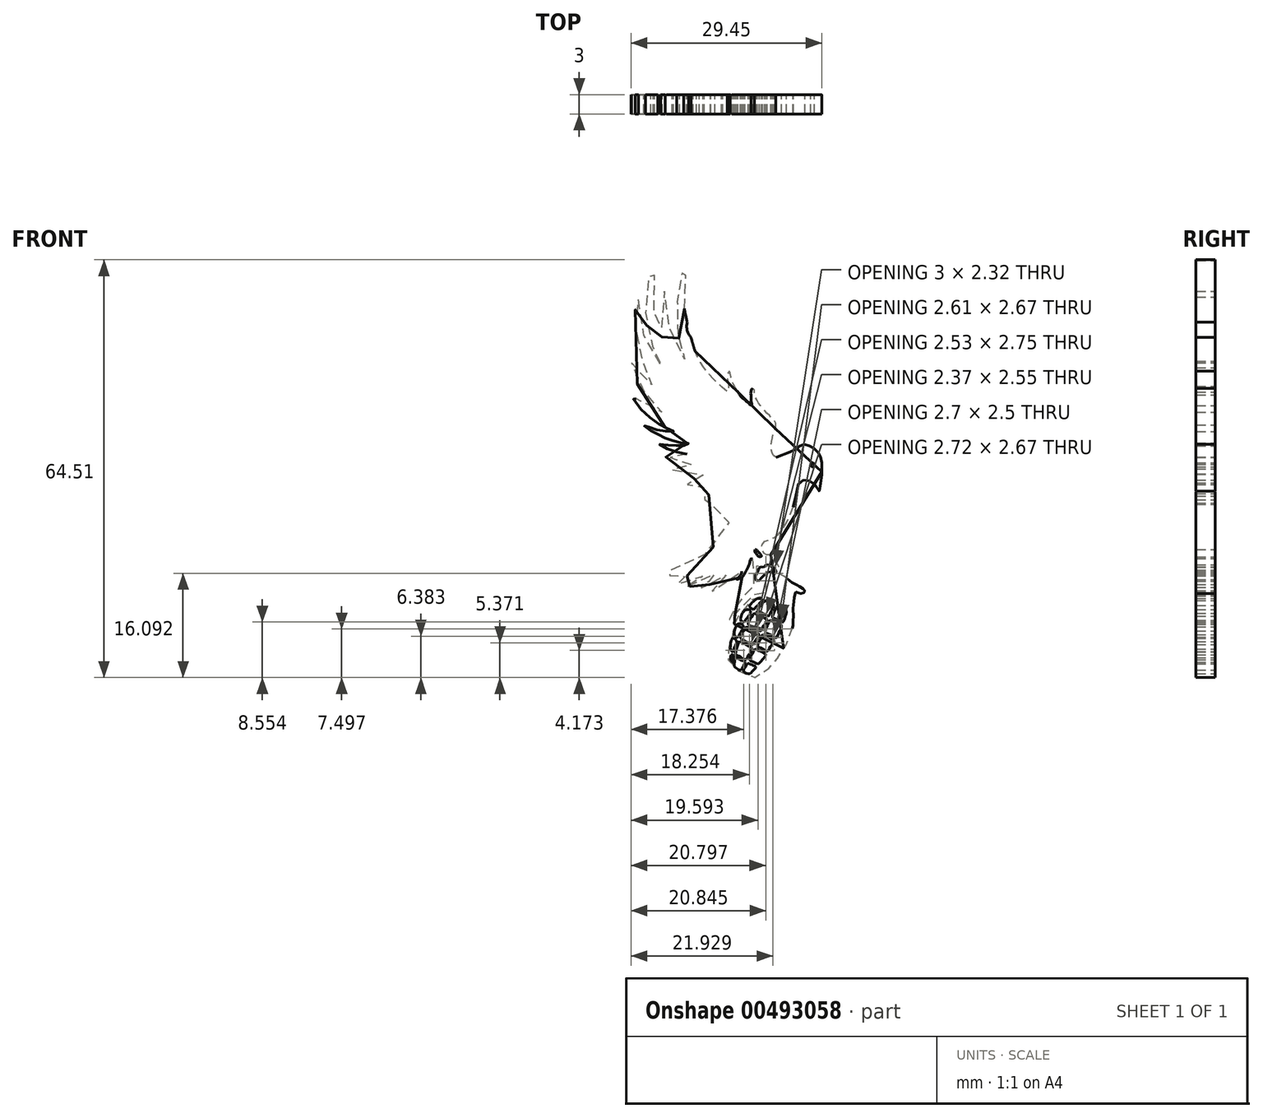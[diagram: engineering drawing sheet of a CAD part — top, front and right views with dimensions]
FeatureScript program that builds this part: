
annotation { "Feature Type Name" : "Feature", "Feature Type Description" : "" }
export const myFeature = defineFeature(function(context is Context, id is Id, definition is map)
    precondition{}
    {
        {
            var Q0;
            Q0=qCreatedBy(makeId("Front.planeOp"),FACE);
            var sketch = newSketch(context, id + "F0", { "sketchPlane" : qUnion([Q0])});
            skFitSpline(sketch, "E0", {"points": [v(10.7, -6.54) * mm, v(10.82, -6.51) * mm, v(10.87, -6.35) * mm, v(10.83, -6.15) * mm, v(10.74, -5.98) * mm, v(10.6, -5.9) * mm, v(10.46, -5.88) * mm, v(10.34, -5.97) * mm, v(10.3, -6.12) * mm, v(10.31, -6.28) * mm, v(10.4, -6.45) * mm, v(10.48, -6.53) * mm, v(10.58, -6.56) * mm, v(10.7, -6.54) * mm]});
            skFitSpline(sketch, "E1", {"points": [v(1.69, -19.3) * mm, v(1.72, -19.8) * mm, v(1.94, -20.05) * mm, v(2.26, -20.4) * mm, v(2.65, -20.35) * mm, v(2.45, -19.97) * mm, v(2.16, -19.65) * mm, v(1.98, -19.4) * mm, v(1.69, -19.3) * mm]});
            skFitSpline(sketch, "E2", {"points": [v(1.88, -24.14) * mm, v(2.38, -24.05) * mm, v(2.74, -23.63) * mm, v(3.12, -23.22) * mm, v(3.52, -22.85) * mm, v(4.1, -22.72) * mm, v(4.6, -23) * mm, v(4.85, -23) * mm, v(4.9, -22.66) * mm, v(4.72, -22.26) * mm, v(4.44, -22) * mm, v(4.24, -21.9) * mm, v(3.88, -21.74) * mm, v(3.66, -21.64) * mm, v(3.38, -21.69) * mm, v(3.17, -21.9) * mm, v(2.98, -22) * mm, v(2.7, -22) * mm, v(2.47, -22) * mm, v(2.33, -22.16) * mm, v(2.18, -22.42) * mm, v(2.05, -22.66) * mm, v(1.94, -22.9) * mm, v(1.84, -23.17) * mm, v(1.77, -23.51) * mm, v(1.75, -23.84) * mm, v(1.88, -24.14) * mm]});
            skFitSpline(sketch, "E3", {"points": [v(5.15, -28) * mm, v(5.57, -28.06) * mm, v(6.04, -28.28) * mm, v(6.42, -28.52) * mm, v(6.48, -29.14) * mm, v(6.34, -29.66) * mm, v(6.18, -30.2) * mm, v(5.94, -30.52) * mm, v(5.51, -30.4) * mm, v(4.93, -30.1) * mm, v(4.53, -29.9) * mm, v(4.33, -29.74) * mm, v(4.51, -29.24) * mm, v(4.77, -28.66) * mm, v(5.15, -28) * mm]});
            skFitSpline(sketch, "E4", {"points": [v(2.05, -28.66) * mm, v(2.3, -28.25) * mm, v(2.68, -27.77) * mm, v(3.02, -27.43) * mm, v(3.32, -27.2) * mm, v(3.73, -27.25) * mm, v(4.05, -27.47) * mm, v(4.4, -27.69) * mm, v(4.59, -27.92) * mm, v(4.43, -28.36) * mm, v(4.2, -28.78) * mm, v(4, -29.15) * mm, v(3.8, -29.56) * mm, v(3.38, -29.45) * mm, v(3.04, -29.27) * mm, v(2.73, -29.09) * mm, v(2.43, -28.96) * mm, v(2.16, -28.8) * mm, v(2.05, -28.66) * mm]});
            skFitSpline(sketch, "E5", {"points": [v(1.48, -28.57) * mm, v(1.77, -28.2) * mm, v(2.04, -27.96) * mm, v(2.29, -27.68) * mm, v(2.55, -27.44) * mm, v(2.85, -27.12) * mm, v(2.77, -26.92) * mm, v(2.39, -26.88) * mm, v(2.05, -26.86) * mm, v(1.73, -27.08) * mm, v(1.39, -27.37) * mm, v(1.14, -27.6) * mm, v(0.9, -27.86) * mm, v(0.83, -28.12) * mm, v(1.02, -28.34) * mm, v(1.33, -28.5) * mm, v(1.48, -28.57) * mm]});
            skFitSpline(sketch, "E6", {"points": [v(-0.02, -30.5) * mm, v(0.21, -30.2) * mm, v(0.43, -29.88) * mm, v(0.71, -29.5) * mm, v(0.92, -29.16) * mm, v(0.96, -28.8) * mm, v(0.73, -28.6) * mm, v(0.4, -28.56) * mm, v(0.15, -28.66) * mm, v(-0.09, -28.9) * mm, v(-0.34, -29.28) * mm, v(-0.5, -29.66) * mm, v(-0.57, -30) * mm, v(-0.52, -30.25) * mm, v(-0.26, -30.44) * mm, v(-0.02, -30.5) * mm]});
            skFitSpline(sketch, "E7", {"points": [v(1.52, -29.18) * mm, v(1.88, -29.3) * mm, v(2.23, -29.46) * mm, v(2.56, -29.6) * mm, v(2.9, -29.78) * mm, v(3.23, -29.94) * mm, v(3.54, -30.13) * mm, v(3.37, -30.52) * mm, v(3.17, -30.8) * mm, v(3, -31.1) * mm, v(2.84, -31.4) * mm, v(2.7, -31.7) * mm, v(2.54, -31.9) * mm, v(2.15, -31.76) * mm, v(1.8, -31.6) * mm, v(1.46, -31.4) * mm, v(1.17, -31.29) * mm, v(0.88, -31.1) * mm, v(0.62, -30.86) * mm, v(0.66, -30.42) * mm, v(0.9, -30.07) * mm, v(1.15, -29.7) * mm, v(1.33, -29.4) * mm, v(1.52, -29.18) * mm]});
            skFitSpline(sketch, "E8", {"points": [v(3.15, -31.96) * mm, v(3.32, -31.47) * mm, v(3.58, -31) * mm, v(3.78, -30.61) * mm, v(4, -30.24) * mm, v(4.47, -30.43) * mm, v(4.79, -30.58) * mm, v(5.24, -30.76) * mm, v(5.73, -30.95) * mm, v(5.68, -31.5) * mm, v(5.46, -31.96) * mm, v(5.26, -32.43) * mm, v(4.96, -32.9) * mm, v(4.45, -32.73) * mm, v(3.91, -32.43) * mm, v(3.56, -32.26) * mm, v(3.15, -31.96) * mm]});
            skFitSpline(sketch, "E9", {"points": [v(1.98, -34.15) * mm, v(2.22, -33.67) * mm, v(2.42, -33.25) * mm, v(2.7, -32.72) * mm, v(2.9, -32.45) * mm, v(3.37, -32.6) * mm, v(3.74, -32.82) * mm, v(4.1, -33) * mm, v(4.45, -33.21) * mm, v(4.68, -33.37) * mm, v(4.48, -33.72) * mm, v(4.24, -34.08) * mm, v(4, -34.42) * mm, v(3.79, -34.75) * mm, v(3.57, -35.03) * mm, v(3.13, -34.83) * mm, v(2.72, -34.6) * mm, v(2.26, -34.36) * mm, v(1.98, -34.15) * mm]});
            skFitSpline(sketch, "E10", {"points": [v(1.36, -33.96) * mm, v(1.55, -33.63) * mm, v(1.82, -33.21) * mm, v(2.09, -32.82) * mm, v(2.34, -32.43) * mm, v(2.04, -32.2) * mm, v(1.67, -32) * mm, v(1.37, -31.8) * mm, v(0.97, -31.58) * mm, v(0.66, -31.38) * mm, v(0.38, -31.25) * mm, v(0.1, -31.44) * mm, v(-0.09, -31.79) * mm, v(-0.19, -32.05) * mm, v(-0.32, -32.34) * mm, v(-0.45, -32.65) * mm, v(-0.6, -32.95) * mm, v(-0.38, -33.15) * mm, v(-0.13, -33.32) * mm, v(0.13, -33.47) * mm, v(0.43, -33.64) * mm, v(0.7, -33.8) * mm, v(1.02, -33.96) * mm, v(1.36, -33.96) * mm]});
            skFitSpline(sketch, "E11", {"points": [v(-0.93, -32.84) * mm, v(-0.75, -32.41) * mm, v(-0.5, -31.97) * mm, v(-0.26, -31.57) * mm, v(-0.12, -31.22) * mm, v(-0.38, -30.85) * mm, v(-0.76, -30.76) * mm, v(-1.13, -30.91) * mm, v(-1.4, -31.42) * mm, v(-1.53, -31.91) * mm, v(-1.56, -32.32) * mm, v(-1.44, -32.67) * mm, v(-1.13, -32.83) * mm, v(-0.93, -32.84) * mm]});
            skFitSpline(sketch, "E12", {"points": [v(-1.73, -35.1) * mm, v(-1.55, -34.61) * mm, v(-1.36, -34.12) * mm, v(-1.16, -33.6) * mm, v(-1.33, -33.18) * mm, v(-1.78, -33.04) * mm, v(-2.07, -33.52) * mm, v(-2.12, -34.19) * mm, v(-2.1, -34.76) * mm, v(-1.73, -35.1) * mm]});
            skFitSpline(sketch, "E13", {"points": [v(-2.02, -35.59) * mm, v(-1.68, -35.6) * mm, v(-1.7, -36.13) * mm, v(-1.76, -36.7) * mm, v(-2.02, -36.45) * mm, v(-2.1, -36) * mm, v(-2.02, -35.59) * mm]});
            skFitSpline(sketch, "E14", {"points": [v(-1.52, -37.35) * mm, v(-1.54, -36.94) * mm, v(-1.47, -36.36) * mm, v(-1.27, -36.03) * mm, v(-0.79, -36.22) * mm, v(-0.42, -36.43) * mm, v(0.1, -36.57) * mm, v(-0.04, -37.14) * mm, v(-0.23, -37.52) * mm, v(-0.45, -37.89) * mm, v(-0.83, -37.9) * mm, v(-1.16, -37.66) * mm, v(-1.52, -37.35) * mm]});
            skFitSpline(sketch, "E15", {"points": [v(0.54, -36.88) * mm, v(0.91, -36.98) * mm, v(1.35, -37.18) * mm, v(1.79, -37.42) * mm, v(1.58, -37.8) * mm, v(1.24, -38.11) * mm, v(0.88, -38.47) * mm, v(0.46, -38.47) * mm, v(0.06, -38.28) * mm, v(-0.1, -37.99) * mm, v(0.16, -37.48) * mm, v(0.37, -37.08) * mm, v(0.54, -36.88) * mm]});
            skFitSpline(sketch, "E16", {"points": [v(0.8, -36.26) * mm, v(1.04, -35.8) * mm, v(1.27, -35.35) * mm, v(1.55, -34.8) * mm, v(1.8, -34.68) * mm, v(2.32, -34.92) * mm, v(2.85, -35.17) * mm, v(3.33, -35.51) * mm, v(3.1, -35.98) * mm, v(2.82, -36.3) * mm, v(2.56, -36.62) * mm, v(2.18, -36.98) * mm, v(1.7, -36.83) * mm, v(1.3, -36.63) * mm, v(0.8, -36.26) * mm]});
            skFitSpline(sketch, "E17", {"points": [v(0.3, -36.27) * mm, v(0.54, -35.85) * mm, v(0.85, -35.37) * mm, v(1.1, -34.87) * mm, v(1.18, -34.51) * mm, v(0.67, -34.18) * mm, v(0.15, -33.9) * mm, v(-0.26, -33.6) * mm, v(-0.8, -33.55) * mm, v(-1.02, -34.06) * mm, v(-1.21, -34.7) * mm, v(-1.29, -35.13) * mm, v(-1.33, -35.55) * mm, v(-0.85, -35.76) * mm, v(-0.38, -36.01) * mm, v(0, -36.26) * mm, v(0.3, -36.27) * mm]});
            skCircle(sketch, "E18", {"center": v(-6.39, 15.14) * mm, "radius": 2.5 * mm});
            skArc(sketch, "E19.trimOffspring", {"start": v(-7.61, 11.37) * mm, "mid": v(-2.47, 16.13) * mm, "end": v(-9.25, 17.92) * mm});
            skFitSpline(sketch, "E20.trimOffspring", {"points": [v(11.64, -10.29) * mm, v(11.75, -9.58) * mm, v(11.84, -8.7) * mm, v(11.95, -7.88) * mm, v(11.98, -7.17) * mm, v(11.98, -6.38) * mm, v(11.9, -5.44) * mm, v(11.67, -4.74) * mm, v(11.3, -4.23) * mm, v(10.7, -3.66) * mm, v(10.17, -3.38) * mm, v(9.6, -3.15) * mm, v(8.86, -3.1) * mm, v(8.36, -3.52) * mm, v(7.85, -3.91) * mm, v(7.28, -4.17) * mm, v(6.6, -4.42) * mm, v(6, -4.65) * mm, v(5.5, -4.85) * mm, v(4.87, -5.1) * mm, v(4.52, -4.8) * mm, v(4.3, -4.37) * mm, v(4.17, -3.82) * mm, v(4.15, -3.18) * mm, v(4.23, -2.52) * mm, v(4.37, -1.93) * mm, v(4.52, -1.4) * mm, v(4.75, -0.8) * mm, v(4.89, -0.23) * mm, v(4.84, 0.33) * mm, v(4.57, 0.7) * mm, v(4.26, 1.02) * mm, v(3.93, 1.36) * mm, v(3.6, 1.69) * mm, v(3.22, 2.1) * mm, v(2.9, 2.47) * mm, v(2.59, 2.8) * mm, v(2.31, 3.17) * mm, v(2.06, 3.59) * mm, v(1.84, 4) * mm, v(1.62, 4.41) * mm, v(1.57, 4.92) * mm, v(1.5, 5.5) * mm, v(1.28, 5.6) * mm, v(1.05, 5.15) * mm, v(1.05, 4.48) * mm, v(1.05, 3.84) * mm, v(1.17, 3.24) * mm, v(1.1, 2.93) * mm, v(0.71, 3.25) * mm, v(0.4, 3.49) * mm, v(0.12, 3.74) * mm, v(-0.2, 4) * mm, v(-0.45, 4.22) * mm, v(-0.65, 4.48) * mm, v(-0.85, 4.87) * mm, v(-1.16, 5.33) * mm, v(-1.45, 5.8) * mm, v(-1.72, 6.3) * mm, v(-1.94, 6.85) * mm, v(-2.08, 7.45) * mm, v(-2.17, 7.99) * mm, v(-2.18, 8.21) * mm, v(-2.5, 8.19) * mm, v(-2.6, 7.62) * mm, v(-2.58, 7.01) * mm, v(-2.5, 6.46) * mm, v(-2.44, 5.92) * mm, v(-2.41, 5.34) * mm, v(-2.45, 5.03) * mm, v(-2.78, 5.25) * mm, v(-3.2, 5.57) * mm, v(-3.68, 6.02) * mm, v(-4.14, 6.43) * mm, v(-4.56, 6.83) * mm, v(-5.11, 7.45) * mm, v(-5.77, 8.16) * mm, v(-6.28, 8.86) * mm, v(-6.84, 9.77) * mm, v(-7.4, 10.79) * mm, v(-9.28, 18.06) * mm, v(-9.32, 19.16) * mm, v(-9.28, 20.44) * mm, v(-9.2, 21.85) * mm, v(-9.01, 23.04) * mm, v(-8.79, 24.45) * mm, v(-8.64, 25.44) * mm, v(-9.16, 24.68) * mm, v(-9.48, 23.78) * mm, v(-9.78, 22.92) * mm, v(-10, 22.06) * mm, v(-10.16, 21.07) * mm, v(-10.26, 20.05) * mm, v(-10.32, 19.15) * mm, v(-10.39, 18.06) * mm, v(-10.44, 16.91) * mm, v(-10.44, 15.82) * mm, v(-10.34, 14.53) * mm, v(-10.06, 13.2) * mm, v(-9.72, 11.96) * mm, v(-9.25, 10.72) * mm, v(-8.87, 9.77) * mm, v(-9.58, 10.53) * mm, v(-10.39, 11.72) * mm, v(-10.91, 12.82) * mm, v(-11.44, 14.44) * mm, v(-11.72, 15.63) * mm, v(-12.06, 16.96) * mm, v(-12.25, 18.77) * mm, v(-12.3, 20.58) * mm, v(-12.77, 19.1) * mm, v(-12.87, 17.53) * mm, v(-12.82, 15.91) * mm, v(-12.77, 14.72) * mm, v(-12.77, 13.49) * mm, v(-13.39, 14.82) * mm, v(-13.77, 16.3) * mm, v(-14, 17.87) * mm, v(-14, 19.58) * mm, v(-13.96, 21.2) * mm, v(-13.92, 22.51) * mm, v(-13.64, 24.07) * mm, v(-13.36, 25.35) * mm, v(-14.08, 24.4) * mm, v(-14.56, 23.31) * mm, v(-15, 21.95) * mm, v(-15.12, 20.47) * mm, v(-15.2, 19.03) * mm, v(-15.24, 17.47) * mm, v(-15.16, 16.14) * mm, v(-14.96, 14.82) * mm, v(-14.64, 13.66) * mm, v(-14.24, 12.26) * mm, v(-13.68, 11.02) * mm, v(-13.2, 10.14) * mm, v(-12.68, 9.34) * mm, v(-12.28, 8.78) * mm, v(-13.12, 9.34) * mm, v(-13.88, 10.3) * mm, v(-14.52, 11.5) * mm, v(-15.12, 12.86) * mm, v(-15.68, 14.26) * mm, v(-16, 15.66) * mm, v(-16.24, 17.07) * mm, v(-16.36, 18.3) * mm, v(-16.4, 19.7) * mm, v(-16.76, 18.55) * mm, v(-16.8, 17.23) * mm, v(-16.84, 15.9) * mm, v(-16.76, 14.5) * mm, v(-16.6, 13.14) * mm, v(-16.32, 11.86) * mm, v(-15.88, 10.38) * mm, v(-15.56, 9.14) * mm, v(-15.04, 7.98) * mm, v(-14.4, 7.01) * mm, v(-13.84, 5.93) * mm, v(-14.76, 6.5) * mm, v(-15.52, 7.21) * mm, v(-16.16, 7.86) * mm, v(-16.92, 8.74) * mm, v(-17.4, 9.54) * mm, v(-17.28, 8.3) * mm, v(-16.92, 7.05) * mm, v(-16.28, 5.93) * mm, v(-15.71, 5.27) * mm, v(-15, 4.4) * mm, v(-14.43, 3.7) * mm, v(-13.8, 3.15) * mm, v(-13.19, 2.55) * mm, v(-12.65, 1.94) * mm, v(-13.56, 2.18) * mm, v(-14.23, 2.45) * mm, v(-15.17, 2.95) * mm, v(-15.91, 3.46) * mm, v(-16.76, 4.03) * mm, v(-17.46, 4.57) * mm, v(-16.72, 3.35) * mm, v(-16.12, 2.58) * mm, v(-15.3, 1.7) * mm, v(-14.4, 0.96) * mm, v(-13.6, 0.32) * mm, v(-12.81, -0.13) * mm, v(-12.24, -0.42) * mm, v(-11.8, -0.63) * mm, v(-11.35, -0.82) * mm, v(-10.92, -1.02) * mm, v(-11.31, -1.1) * mm, v(-11.9, -1.05) * mm, v(-12.44, -1.02) * mm, v(-13.08, -0.91) * mm, v(-13.67, -0.77) * mm, v(-14.29, -0.6) * mm, v(-14.81, -0.39) * mm, v(-15.2, -0.2) * mm, v(-15.54, -0.07) * mm, v(-15.27, -0.4) * mm, v(-14.9, -0.68) * mm, v(-14.46, -0.93) * mm, v(-14, -1.17) * mm, v(-13.5, -1.43) * mm, v(-13.03, -1.68) * mm, v(-12.62, -1.9) * mm, v(-12.09, -2.14) * mm, v(-11.66, -2.3) * mm, v(-11.16, -2.46) * mm, v(-10.59, -2.63) * mm, v(-10.12, -2.73) * mm, v(-9.56, -2.83) * mm, v(-9, -2.88) * mm, v(-8.56, -2.95) * mm, v(-8.66, -3.24) * mm, v(-9, -3.27) * mm, v(-9.42, -3.27) * mm, v(-9.94, -3.26) * mm, v(-10.38, -3.26) * mm, v(-10.87, -3.24) * mm, v(-11.44, -3.19) * mm, v(-12, -3.15) * mm, v(-12.5, -3.13) * mm, v(-13.14, -3.1) * mm, v(-12.5, -3.52) * mm, v(-11.68, -3.85) * mm, v(-10.84, -4.14) * mm, v(-9.98, -4.3) * mm, v(-9.15, -4.5) * mm, v(-8.3, -4.6) * mm, v(-7.87, -4.69) * mm, v(-8.2, -5) * mm, v(-8.96, -5.07) * mm, v(-9.53, -5.11) * mm, v(-10.27, -5.07) * mm, v(-10.96, -5.07) * mm, v(-11.44, -5.07) * mm, v(-12.25, -5.07) * mm, v(-11.53, -5.64) * mm, v(-11.1, -5.85) * mm, v(-10.39, -5.97) * mm, v(-9.48, -6.07) * mm, v(-8.65, -6.16) * mm, v(-8.03, -6.16) * mm, v(-7.39, -6.16) * mm, v(-7.65, -6.57) * mm, v(-8.27, -6.76) * mm, v(-8.91, -6.85) * mm, v(-9.84, -6.88) * mm, v(-10.53, -6.88) * mm, v(-11.13, -6.97) * mm, v(-10.53, -7.35) * mm, v(-9.91, -7.61) * mm, v(-9.08, -7.7) * mm, v(-8.25, -7.69) * mm, v(-7.41, -7.69) * mm, v(-6.72, -7.64) * mm, v(-6.37, -7.78) * mm, v(-6.87, -8.02) * mm, v(-7.5, -8.26) * mm, v(-8.08, -8.47) * mm, v(-8.8, -8.7) * mm, v(-9.34, -8.85) * mm, v(-9.98, -8.97) * mm, v(-8.98, -9.23) * mm, v(-7.94, -9.23) * mm, v(-7.08, -9.19) * mm, v(-6.32, -9.11) * mm, v(-5.75, -9.04) * mm, v(-5.15, -9.11) * mm, v(-5.53, -9.45) * mm, v(-6.17, -9.66) * mm, v(-6.84, -9.9) * mm, v(-7.6, -10.11) * mm, v(-8.2, -10.35) * mm, v(-8.75, -10.61) * mm, v(-7.65, -10.64) * mm, v(-6.67, -10.57) * mm, v(-5.84, -10.47) * mm, v(-5.06, -10.38) * mm, v(-4.53, -10.35) * mm, v(-5.06, -10.72) * mm, v(-5.77, -10.96) * mm, v(-6.34, -11.23) * mm, v(-6.92, -11.56) * mm, v(-5.8, -11.53) * mm, v(-4.83, -11.46) * mm, v(-3.92, -11.33) * mm, v(-3.31, -11.06) * mm, v(-3.58, -11.63) * mm, v(-4.42, -11.93) * mm, v(-5.2, -12.27) * mm, v(-4.02, -12.34) * mm, v(-2.98, -12.3) * mm, v(-1.97, -12.2) * mm, v(-1.97, -13.18) * mm, v(-2.09, -14.1) * mm, v(-2.33, -15.06) * mm, v(-2.77, -16.02) * mm, v(-3.25, -17.01) * mm, v(-3.94, -17.92) * mm, v(-4.75, -18.87) * mm, v(-5.6, -19.66) * mm, v(-6.46, -20.37) * mm, v(-7.4, -20.97) * mm, v(-8.49, -21.51) * mm, v(-9.63, -21.94) * mm, v(-10.4, -22.26) * mm, v(-11.18, -22.47) * mm, v(-12.04, -22.73) * mm, v(-12.82, -22.84) * mm, v(-13.6, -22.87) * mm, v(-14.43, -22.94) * mm, v(-13.07, -23.31) * mm, v(-11.87, -23.33) * mm, v(-10.95, -23.17) * mm, v(-10.09, -22.97) * mm, v(-9.27, -22.75) * mm, v(-8.47, -22.67) * mm, v(-7.99, -22.7) * mm, v(-8.23, -23.11) * mm, v(-8.97, -23.4) * mm, v(-9.6, -23.7) * mm, v(-10.33, -23.96) * mm, v(-11.17, -24.2) * mm, v(-11.8, -24.44) * mm, v(-12.25, -24.66) * mm, v(-11.1, -24.68) * mm, v(-10.17, -24.58) * mm, v(-9.39, -24.34) * mm, v(-8.63, -24.02) * mm, v(-7.85, -23.68) * mm, v(-7.17, -23.35) * mm, v(-6.63, -23.05) * mm, v(-6.2, -22.97) * mm, v(-6.34, -23.4) * mm, v(-6.89, -23.7) * mm, v(-7.47, -23.98) * mm, v(-8.13, -24.32) * mm, v(-8.77, -24.62) * mm, v(-9.39, -24.84) * mm, v(-10, -25.04) * mm, v(-9.27, -25.14) * mm, v(-8.45, -25.04) * mm, v(-7.65, -24.82) * mm, v(-6.97, -24.5) * mm, v(-6.28, -24.18) * mm, v(-5.66, -23.86) * mm, v(-5.24, -23.54) * mm, v(-4.8, -23.22) * mm, v(-4.42, -22.97) * mm, v(-4.04, -22.68) * mm, v(-3.6, -22.48) * mm, v(-3.53, -22.75) * mm, v(-3.81, -23.1) * mm, v(-4.18, -23.4) * mm, v(-4.5, -23.68) * mm, v(-4.89, -23.94) * mm, v(-5.35, -24.2) * mm, v(-5.8, -24.42) * mm, v(-6.3, -24.67) * mm, v(-6.7, -24.9) * mm, v(-7.08, -25.05) * mm, v(-7.6, -25.28) * mm, v(-7.96, -25.62) * mm, v(-7.35, -25.45) * mm, v(-6.8, -25.3) * mm, v(-6.25, -25.1) * mm, v(-5.83, -24.95) * mm, v(-5.42, -24.78) * mm, v(-5.03, -24.56) * mm, v(-4.5, -24.3) * mm, v(-4.05, -24.08) * mm, v(-3.55, -23.81) * mm, v(-3.13, -23.5) * mm, v(-2.63, -23.19) * mm, v(-2.63, -23.54) * mm, v(-3.09, -23.94) * mm, v(-3.46, -24.26) * mm, v(-3.9, -24.67) * mm, v(-4.3, -25) * mm, v(-4.72, -25.27) * mm, v(-5.25, -25.73) * mm, v(-4.34, -25.6) * mm, v(-3.53, -25.26) * mm, v(-2.65, -24.79) * mm, v(-2.01, -24.25) * mm, v(-1.37, -23.64) * mm, v(-0.76, -22.92) * mm, v(-0.38, -22.7) * mm, v(-0.45, -23.07) * mm, v(-0.88, -23.59) * mm, v(-1.17, -23.92) * mm, v(-0.45, -23.64) * mm, v(-0.08, -23.27) * mm, v(0.28, -22.67) * mm, v(0.57, -22.08) * mm, v(0.8, -21.5) * mm, v(1.02, -20.73) * mm, v(1.47, -20.99) * mm, v(1.49, -21.85) * mm, v(1.45, -22.55) * mm, v(1.3, -23.31) * mm, v(1.33, -24.13) * mm, v(1.49, -24.91) * mm, v(0.9, -25.36) * mm, v(0.35, -25.98) * mm, v(-0.33, -26.78) * mm, v(-0.81, -27.51) * mm, v(-1.18, -27.98) * mm, v(-1.54, -28.54) * mm, v(-1.88, -29.18) * mm, v(-2.18, -29.82) * mm, v(-2.53, -30.9) * mm, v(-1.91, -29.96) * mm, v(-1.22, -29.03) * mm, v(-0.6, -28.3) * mm, v(0, -27.8) * mm, v(0.57, -27.19) * mm, v(1.22, -26.54) * mm, v(1.78, -26.03) * mm, v(2.2, -25.71) * mm, v(2.4, -25.98) * mm, v(2.92, -26) * mm, v(3.53, -26.06) * mm, v(3.43, -26.27) * mm, v(3.08, -26.3) * mm, v(2.8, -26.48) * mm, v(2.27, -26.48) * mm, v(1.79, -26.62) * mm, v(1.42, -26.85) * mm, v(1.07, -27.2) * mm, v(0.69, -27.57) * mm, v(0.42, -28.15) * mm, v(0.11, -28.33) * mm, v(-0.24, -28.6) * mm, v(-0.56, -29.01) * mm, v(-0.81, -29.48) * mm, v(-0.98, -29.88) * mm, v(-1, -30.34) * mm, v(-1.33, -30.5) * mm, v(-1.6, -30.97) * mm, v(-1.76, -31.61) * mm, v(-1.83, -32.28) * mm, v(-1.85, -32.76) * mm, v(-2.1, -32.91) * mm, v(-2.28, -33.47) * mm, v(-2.35, -34.1) * mm, v(-2.36, -34.7) * mm, v(-2.34, -35.22) * mm, v(-2.47, -35.89) * mm, v(-2.34, -36.78) * mm, v(-1.73, -37.52) * mm, v(-0.7, -38.14) * mm, v(0.6, -38.82) * mm, v(1.62, -39.05) * mm, v(2.8, -38.37) * mm, v(3.43, -37.92) * mm, v(4.4, -37.18) * mm, v(4.62, -36.62) * mm, v(4.95, -36.26) * mm, v(5.88, -35.33) * mm, v(6.12, -34.45) * mm, v(6.85, -33.5) * mm, v(7.13, -32.04) * mm, v(7.5, -31.2) * mm, v(7.56, -30.21) * mm, v(7.62, -29.35) * mm, v(7.54, -28.32) * mm, v(7.74, -26.88) * mm, v(7.98, -25.88) * mm, v(8.59, -26.12) * mm, v(9.36, -25.81) * mm, v(8.62, -25.04) * mm, v(7.65, -24.57) * mm, v(6.87, -24) * mm, v(6.1, -23.42) * mm, v(5.6, -23.05) * mm, v(5.36, -22) * mm, v(4.95, -21.37) * mm, v(4.58, -20.66) * mm, v(4.35, -20.23) * mm, v(3.57, -20.12) * mm, v(2.87, -19.65) * mm, v(2.87, -18.3) * mm, v(4.28, -17.63) * mm, v(5.66, -16.49) * mm, v(6.55, -15.07) * mm, v(7.35, -13.31) * mm, v(7.91, -11.28) * mm, v(8.2, -9.86) * mm, v(8.47, -9.06) * mm, v(9.24, -8.58) * mm, v(10.12, -8.74) * mm, v(10.92, -9.34) * mm, v(11.64, -10.29) * mm]});
            skSolve(sketch);
        }
        {
            var Q0;
            Q0=makeQuery(id+"F0.imprint","IMPRINT",FACE,{"disambiguationData":[TD([[makeQuery(id+"F0.imprint","IMPRINT",EDGE,{"derivedFrom":sQuery(id+"F0.wireOp",EDGE,"E0")}),-1.0]])]});
            extrude(context, id + "F1", {"entities" : qUnion([Q0]), "depth" : 3 * mm});
        }
    });
